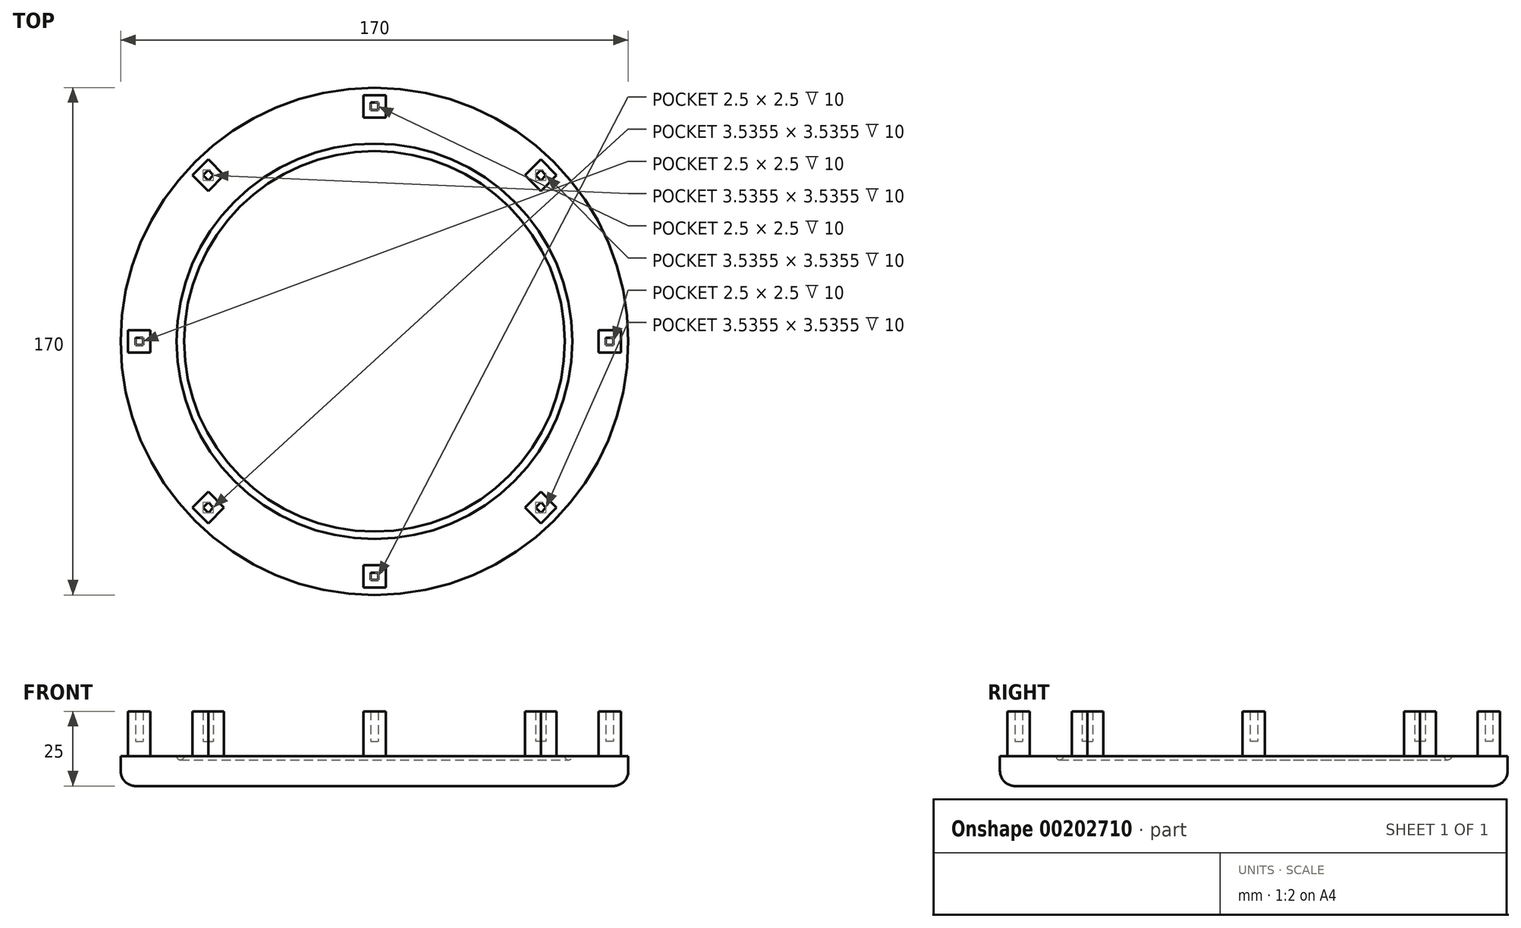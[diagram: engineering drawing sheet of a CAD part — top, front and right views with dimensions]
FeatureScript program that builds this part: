
annotation { "Feature Type Name" : "Feature", "Feature Type Description" : "" }
export const myFeature = defineFeature(function(context is Context, id is Id, definition is map)
    precondition{}
    {
        {
            var Q0;
            Q0=qCreatedBy(makeId("Top.planeOp"),FACE);
            var sketch = newSketch(context, id + "F0", { "sketchPlane" : qUnion([Q0])});
            skCircle(sketch, "E0", {"center": v(0, 0) * mm, "radius": 85 * mm});
            skLineSegment(sketch, "E1", {"start": v(0, -85) * mm, "end": v(0, -78.75) * mm});
            skPoint(sketch, "E2.middle", {"position": v(0, -78.75) * mm});
            skLineSegment(sketch, "E3.bottom", {"start": v(-1.25, -80) * mm, "end": v(1.25, -80) * mm});
            skLineSegment(sketch, "E3.top", {"start": v(-1.25, -77.5) * mm, "end": v(1.25, -77.5) * mm});
            skLineSegment(sketch, "E3.left", {"start": v(-1.25, -80) * mm, "end": v(-1.25, -77.5) * mm});
            skLineSegment(sketch, "E3.right", {"start": v(1.25, -80) * mm, "end": v(1.25, -77.5) * mm});
            skLineSegment(sketch, "E4.bottom", {"start": v(-3.75, -82.5) * mm, "end": v(3.75, -82.5) * mm});
            skLineSegment(sketch, "E4.top", {"start": v(-3.75, -75) * mm, "end": v(3.75, -75) * mm});
            skLineSegment(sketch, "E4.left", {"start": v(-3.75, -82.5) * mm, "end": v(-3.75, -75) * mm});
            skLineSegment(sketch, "E4.right", {"start": v(3.75, -82.5) * mm, "end": v(3.75, -75) * mm});
            skSolve(sketch);
        }
        {
            var Q0;
            Q0=makeQuery(id+"F0.imprint","IMPRINT",FACE,{"disambiguationData":[TD([[makeQuery(id+"F0.imprint","IMPRINT",EDGE,{"derivedFrom":sQuery(id+"F0.wireOp",EDGE,"E0")}),1.0]])]});
            extrude(context, id + "F1", {"entities" : qUnion([Q0]), "depth" : 5 * mm});
        }
        {
            var Q0;
            Q0=makeQuery(id+"F0.imprint","IMPRINT",FACE,{"disambiguationData":[TD([[makeQuery(id+"F0.imprint","IMPRINT",EDGE,{"derivedFrom":sQuery(id+"F0.wireOp",EDGE,"E3.top")}),1.0]])]});
            extrude(context, id + "F2", {"entities" : qUnion([Q0]), "depth" : 20 * mm});
        }
        {
            var Q0;
            Q0=makeQuery(id+"F0.imprint","IMPRINT",FACE,{"disambiguationData":[TD([[makeQuery(id+"F0.imprint","IMPRINT",EDGE,{"derivedFrom":sQuery(id+"F0.wireOp",EDGE,"E3.top")}),-1.0]])]});
            extrude(context, id + "F3", {"entities" : qUnion([Q0]), "operationType" : NewBodyOperationType.ADD, "depth" : 10 * mm});
        }
        {
            var Q0;
            Q0=qCreatedBy(makeId("Right.planeOp"),FACE);
            var sketch = newSketch(context, id + "F4", { "sketchPlane" : qUnion([Q0])});
            skLineSegment(sketch, "E5", {"start": v(0, 0) * mm, "end": v(0, 28.2) * mm});
            skSolve(sketch);
        }
        {
            var Q0;
            Q0=makeQuery(id+"F2.opExtrude","SWEPT_BODY",BODY,{"disambiguationData":[OSD([sQuery(id+"F0.wireOp",EDGE,"E3.bottom"),sQuery(id+"F0.wireOp",EDGE,"E3.top"),sQuery(id+"F0.wireOp",EDGE,"E3.left"),sQuery(id+"F0.wireOp",EDGE,"E3.right"),sQuery(id+"F0.wireOp",EDGE,"E4.bottom"),sQuery(id+"F0.wireOp",EDGE,"E4.top"),sQuery(id+"F0.wireOp",EDGE,"E4.left"),sQuery(id+"F0.wireOp",EDGE,"E4.right")])]});
            var Q1;
            Q1=sQuery(id+"F4.wireOp",EDGE,"E5");
            circularPattern(context, id + "F5", {"entities" : qUnion([Q0]), "axis" : qUnion([Q1]), "angle" : 360 * degree, "instanceCount" : 8, "equalSpace" : true});
        }
        {
            var Q0;
            Q0=makeQuery(id+"F0.imprint","IMPRINT",FACE,{"disambiguationData":[TD([[makeQuery(id+"F0.imprint","IMPRINT",EDGE,{"derivedFrom":sQuery(id+"F0.wireOp",EDGE,"E0")}),1.0]])]});
            var sketch = newSketch(context, id + "F6", { "sketchPlane" : qUnion([Q0])});
            skPoint(sketch, "E6.middle", {"position": v(0, 0) * mm});
            skSolve(sketch);
        }
        {
            var Q0;
            {var subQ0=sQuery(id+"F6.wireOp",EDGE,"E6.left");var subQ1=makeQuery(id+"F0.imprint","IMPRINT",EDGE,{"derivedFrom":sQuery(id+"F0.wireOp",EDGE,"E0")});var subQ2=makeQuery(id+"F6.imprint","INTERSECT",VERTEX,{"disambiguationData":[OD(0.0)],"derivedFrom":[subQ1,subQ0]});Q0=makeQuery(id+"F6.imprint","IMPRINT",FACE,{"disambiguationData":[TD([[makeQuery(id+"F6.imprint","IMPRINT",EDGE,{"disambiguationData":[TD([[subQ2,-1.0]])],"derivedFrom":subQ0}),1.0]])]});}
            var Q1;
            Q1=makeQuery(id+"F6.imprint","IMPRINT",FACE,{"disambiguationData":[TD([[makeQuery(id+"F6.imprint","IMPRINT",EDGE,{"derivedFrom":makeQuery(id+"F0.imprint","IMPRINT",EDGE,{"derivedFrom":sQuery(id+"F0.wireOp",EDGE,"E4.top")})}),1.0]])]});
            var Q2;
            Q2=makeQuery(id+"F0.imprint","IMPRINT",FACE,{"disambiguationData":[TD([[makeQuery(id+"F0.imprint","IMPRINT",EDGE,{"derivedFrom":sQuery(id+"F0.wireOp",EDGE,"E0")}),1.0]])]});
            var Q3;
            Q3=makeQuery(id+"F0.imprint","IMPRINT",FACE,{"disambiguationData":[TD([[makeQuery(id+"F0.imprint","IMPRINT",EDGE,{"derivedFrom":sQuery(id+"F0.wireOp",EDGE,"E3.top")}),1.0]])]});
            var Q4;
            Q4=makeQuery(id+"F0.imprint","IMPRINT",FACE,{"disambiguationData":[TD([[makeQuery(id+"F0.imprint","IMPRINT",EDGE,{"derivedFrom":sQuery(id+"F0.wireOp",EDGE,"E3.top")}),-1.0]])]});
            extrude(context, id + "F7", {"entities" : qUnion([Q0, Q1, Q2, Q3, Q4]), "operationType" : NewBodyOperationType.ADD, "oppositeDirection" : true, "depth" : 5 * mm});
        }
        {
            var Q0;
            {var subQ0=sQuery(id+"F0.wireOp",EDGE,"E0");Q0=makeQuery(id+"F7.opExtrude","CAP_EDGE",EDGE,{"disambiguationData":[OSD([subQ0]),TDD([makeQuery(id+"F0.imprint","IMPRINT",EDGE,{"derivedFrom":subQ0})])],"isStart":false});}
            var Q1;
            Q1=makeQuery(id+"FZzV59cS7BsCCKl_2.opExtrude","CAP_EDGE",EDGE,{"disambiguationData":[OSD([sQuery(id+"F6.wireOp",EDGE,"E6.left")])],"isStart":true});
            var Q2;
            Q2=makeQuery(id+"FZzV59cS7BsCCKl_2.opExtrude","CAP_EDGE",EDGE,{"disambiguationData":[OSD([sQuery(id+"F6.wireOp",EDGE,"E6.bottom")])],"isStart":true});
            var Q3;
            Q3=makeQuery(id+"FZzV59cS7BsCCKl_2.opExtrude","CAP_EDGE",EDGE,{"disambiguationData":[OSD([sQuery(id+"F6.wireOp",EDGE,"E6.right")])],"isStart":true});
            fillet(context, id + "F8", {"entities" : qUnion([Q0, Q1, Q2, Q3]), "radius" : 5 * mm, "tangentPropagation" : true, "allowEdgeOverflow" : false});
        }
        {
            var Q0;
            Q0=qCreatedBy(makeId("Right.planeOp"),FACE);
            var sketch = newSketch(context, id + "F9", { "sketchPlane" : qUnion([Q0])});
            skLineSegment(sketch, "E7", {"start": v(0, 0) * mm, "end": v(0, 5) * mm});
            skLineSegment(sketch, "E8", {"start": v(0, 5) * mm, "end": v(65, 5) * mm});
            skCircle(sketch, "E9", {"center": v(65, 5) * mm, "radius": 1.25 * mm});
            skSolve(sketch);
        }
        {
            var Q0;
            Q0=makeQuery(id+"F9.imprint","IMPRINT",FACE,{"disambiguationData":[TD([[makeQuery(id+"F9.imprint","IMPRINT",EDGE,{"derivedFrom":sQuery(id+"F9.wireOp",EDGE,"E9")}),1.0]])]});
            var Q1;
            Q1=sQuery(id+"F9.wireOp",EDGE,"E7");
            revolve(context, id + "F10", {"operationType" : NewBodyOperationType.REMOVE, "entities" : qUnion([Q0]), "axis" : qUnion([Q1]), "revolveType" : RevolveType.FULL, "oppositeDirection" : true});
        }
    });
